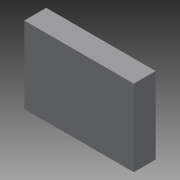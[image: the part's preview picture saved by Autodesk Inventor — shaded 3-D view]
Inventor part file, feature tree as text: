
AUTODESK INVENTOR PART (.ipt)
format: ipt  version: 2014 (Build 180170000, 170)  size: 68,608 bytes
history: native  units: mm
features: other x1, extrude x1, sketch x1
ambient origin geometry x8: Origin, YZ Plane, XZ Plane, XY Plane, X Axis, Y Axis, Z Axis, Center Point
bodies: Body1 (feature_tree)
feature tree (3):
  other  "ソリッド1"
  extrude  "押し出し1"  Depth=100.0mm
  sketch  "スケッチ1"
